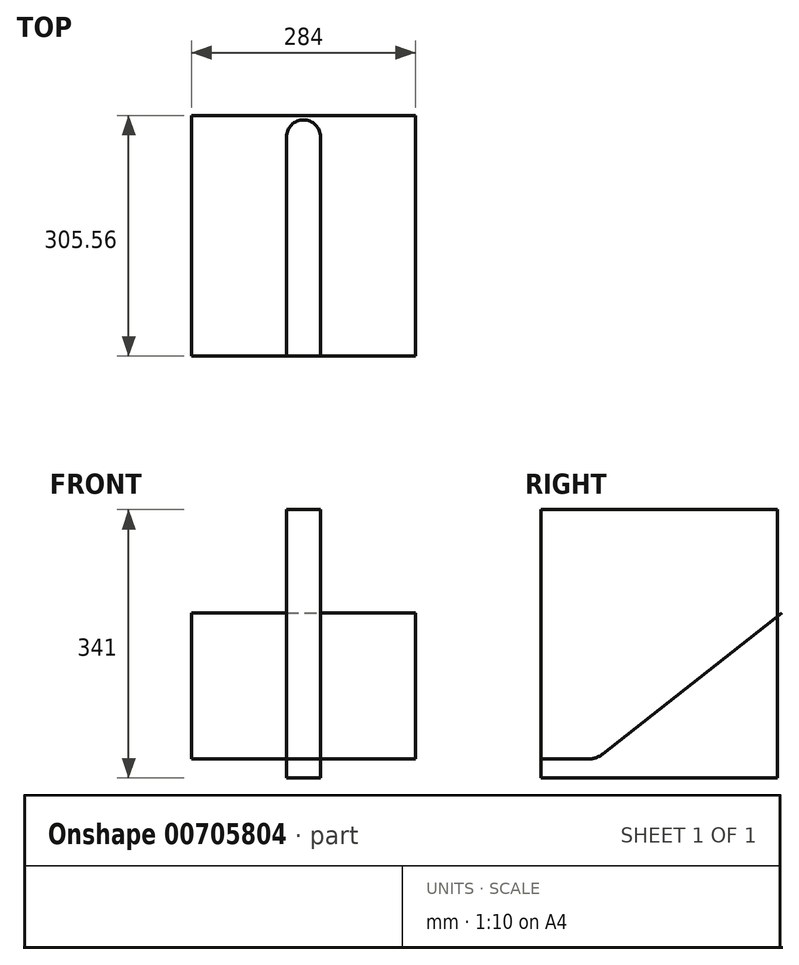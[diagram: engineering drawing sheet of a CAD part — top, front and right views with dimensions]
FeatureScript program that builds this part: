
annotation { "Feature Type Name" : "Feature", "Feature Type Description" : "" }
export const myFeature = defineFeature(function(context is Context, id is Id, definition is map)
    precondition{}
    {
        {
            var Q0;
            Q0=qCreatedBy(makeId("Top.planeOp"),FACE);
            var sketch = newSketch(context, id + "F0", { "sketchPlane" : qUnion([Q0])});
            skLineSegment(sketch, "E0", {"start": v(-21.5, 0) * mm, "end": v(-21.5, 278.5) * mm});
            skLineSegment(sketch, "E1", {"start": v(0, 300) * mm, "end": v(0, 300) * mm});
            skLineSegment(sketch, "E2", {"start": v(21.5, 278.5) * mm, "end": v(21.5, 0) * mm});
            skPoint(sketch, "E3.visualSharp", {"position": v(-21.5, 300) * mm});
            skArc(sketch, "E3.filletArc", {"start": v(0, 300) * mm, "mid": v(-15.2, 293.7) * mm, "end": v(-21.5, 278.5) * mm});
            skPoint(sketch, "E4.visualSharp", {"position": v(21.5, 300) * mm});
            skArc(sketch, "E4.filletArc", {"start": v(21.5, 278.5) * mm, "mid": v(15.2, 293.7) * mm, "end": v(0, 300) * mm});
            skSolve(sketch);
        }
        {
            var Q0;
            Q0 = qSketchRegion(id + "F0", true);
            var Q1;
            Q1=sQuery(id+"F0.wireOp",EDGE,"E0");
            var Q2;
            Q2=sQuery(id+"F0.wireOp",EDGE,"E3.filletArc");
            var Q3;
            Q3=sQuery(id+"F0.wireOp",EDGE,"E4.filletArc");
            var Q4;
            Q4=sQuery(id+"F0.wireOp",EDGE,"E2");
            extrude(context, id + "F1", {"entities" : qUnion([Q0]), "bodyType" : ToolBodyType.SURFACE, "surfaceEntities" : qUnion([Q1, Q2, Q3, Q4]), "depth" : 341 * mm, "offsetDistance" : 25 * mm});
        }
        {
            var Q0;
            Q0=qCreatedBy(makeId("Right.planeOp"),FACE);
            var sketch = newSketch(context, id + "F2", { "sketchPlane" : qUnion([Q0])});
            skLineSegment(sketch, "E5", {"start": v(0, 24) * mm, "end": v(59.6, 24) * mm});
            skLineSegment(sketch, "E6", {"start": v(78.17, 30.43) * mm, "end": v(305.56, 209.76) * mm});
            skPoint(sketch, "E7.visualSharp", {"position": v(70, 24) * mm});
            skArc(sketch, "E7.filletArc", {"start": v(59.6, 24) * mm, "mid": v(69.43, 25.65) * mm, "end": v(78.17, 30.43) * mm});
            skSolve(sketch);
        }
        {
            var Q0;
            Q0=sQuery(id+"F2.wireOp",EDGE,"E5");
            var Q1;
            Q1=sQuery(id+"F2.wireOp",EDGE,"E7.filletArc");
            var Q2;
            Q2=sQuery(id+"F2.wireOp",EDGE,"E6");
            extrude(context, id + "F3", {"bodyType" : ToolBodyType.SURFACE, "surfaceEntities" : qUnion([Q0, Q1, Q2]), "endBound" : BoundingType.SYMMETRIC, "depth" : 284 * mm, "offsetDistance" : 25 * mm});
        }
    });
